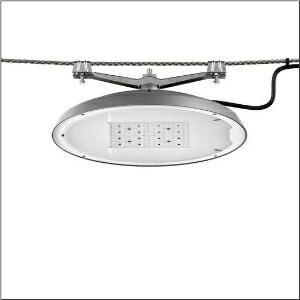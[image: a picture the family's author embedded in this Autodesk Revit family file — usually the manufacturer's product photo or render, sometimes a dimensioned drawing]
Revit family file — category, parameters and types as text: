
# Revit family: dl_50_iq_mini___st1_0s_5xa248w21f08me_e4e8
name_source: partatom
category: Lighting Fixtures
units: mm (PartAtom-declared; Revit-internal decimal feet)

## family parameters
Cut with Voids When Loaded = No
Host = Face
Light Source = No
Part Type = Normal
Room Calculation Point = No
Round Connector Dimension = Use Diameter
Shared = No

## types (1)
- --- (1 x LED, 12600 lm, 103.8 W, 2200K)
    Apparent Load = 104 VA
    CIE Flux Codes = 37 72 97 100 100
    Color Rendering = 70
    Color Temperature = 2200K
    Default Elevation = 1800 mm
    Description = DL 50 iQ mini, catenary luminaire, primary light control with lens, of PMMA, primary optical cover: cover, of toughened safety glass, transparent, light distribution: ST1.0s, light emission: direct distribution, primary light characteristic: symmetric, installation type: suspended mounting, LED, High Power LED, rated luminous flux: 12.600lm, luminous efficacy: 121lm/W, light colour: 722, colour temperature: 2200K, control gear: iQ Street-Remote, control: optimised constant luminous flux control (CLO 2.0), Desk-Remote (wireless, voltage-free reading and setting of iQ features in the workshop via application-optimized NFC function/RFID function), Light-Fading, Smart-Wire, Night-Set, Lumen-Switch, Temp-Guard, Auto-Match, Street-Remote, mains connection: 230..240V, AC, 50/60Hz, start of lifetime: 104W, end of service life: 114W, reduction: 46W, luminaire housing, of diecast aluminium, powder-coated, SITECO metallic grey (DB 702S), diameter: 500mm, height: 115mm, mounting height: 4..12m, protection rating (complete): IP66, insulation class (complete): insulation class II (safety insulation), certification: CE, ENEC, ENEC+, VDE, impact resistance: IK08, permissible operating ambient temperature for outdoor applications: -25..+40°C, standard-compliant lighting for roads and squares, packaging unit: 1 piece

Light Distribution: ST1.0s
    Height = 124 mm  [stored 0.406824 ft]
    Lamp = 1 x LED
    Lamp Light Flux = 12600 lm
    Lamp Power = 103.8 W
    Lamp count = 1
    Length = 500 mm
    Luminous efficacy = 121 lm/W
    Manufacturer = Siteco
    ModVariant = No
    Model = 5XA248W21F08ME
    Number of Poles = 1
    OnlyDefault = Yes
    Power Factor = 1
    Product Name = DL 50 iQ mini | ST1.0s
    Product group = catenary luminaire
    ProductGroupID = 6300
    Protection Class = Protection class II
    Protection Degree = IP 66
    RLX_Detail_Level = 1
    RLX_Emergency_Light_Flux = 0 lm
    RLX_Emergency_Type = 0
    RLX_Emergency_Type_DB = No
    RlxData = <blob elided: 126973 chars, md5=cec51fe7>
    Socket = socket
    Standby Power = 0 W
    System Light Flux = 12600 lm
    System Power = 104 W
    Type Comments = factory setting: luminous flux: 100 % | dim-lin: 254 | 545 mA
    Type Image = l_1251783.jpg
    URL = http://relux.com
    VarID = @adj_139945
    Voltage = 0 V
    Weight = 0.00 kg
    Width = 0 mm  [stored 0 ft]

note: [stored X ft] marks values corroborated as IEEE doubles in the binary element streams (Revit-internal decimal feet)

## geometry (parser evidence)
native form markers: Blend x4, Sweep x13
no freeform markers — native parametric forms only
